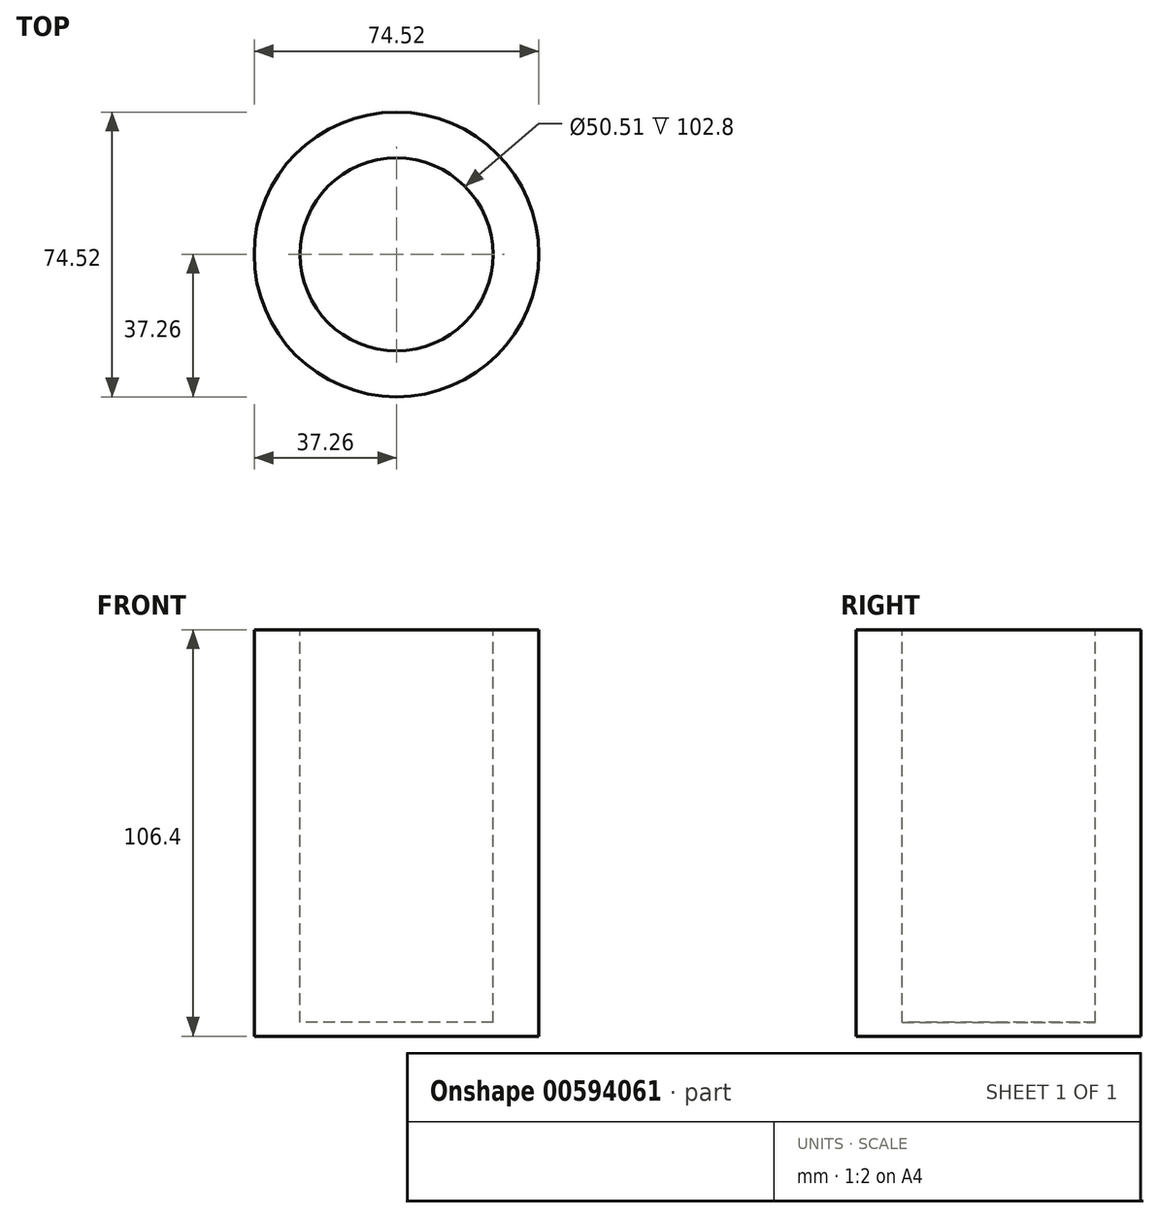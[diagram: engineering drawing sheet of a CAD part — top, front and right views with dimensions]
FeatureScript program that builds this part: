
annotation { "Feature Type Name" : "Feature", "Feature Type Description" : "" }
export const myFeature = defineFeature(function(context is Context, id is Id, definition is map)
    precondition{}
    {
        {
            var Q0;
            Q0=qCreatedBy(makeId("Top.planeOp"),FACE);
            var sketch = newSketch(context, id + "F0", { "sketchPlane" : qUnion([Q0])});
            skCircle(sketch, "E0", {"center": v(0, 0) * mm, "radius": 37.26 * mm});
            skSolve(sketch);
        }
        {
            var Q0;
            Q0 = qSketchRegion(id + "F2", true);
            var Q1;
            Q1=makeQuery(id+"F0.imprint","IMPRINT",FACE,{"disambiguationData":[TD([[makeQuery(id+"F0.imprint","IMPRINT",EDGE,{"derivedFrom":sQuery(id+"F0.wireOp",EDGE,"E0")}),1.0]])]});
            extrude(context, id + "F1", {"entities" : qUnion([Q0, Q1]), "depth" : 106.4 * mm, "offsetDistance" : 25 * mm});
        }
        {
            var Q0;
            Q0=makeQuery(id+"F1.opExtrude","CAP_FACE",FACE,{"disambiguationData":[OSD([sQuery(id+"F0.wireOp",EDGE,"E0")])],"isStart":false});
            var sketch = newSketch(context, id + "F2", { "sketchPlane" : qUnion([Q0])});
            skCircle(sketch, "E1.cCircle", {"center": v(0, 0) * mm, "radius": 28.44 * mm, "construction": true});
            skLineSegment(sketch, "E1.0", {"start": v(30.45, -12.3) * mm, "end": v(4.57, -32.52) * mm});
            skLineSegment(sketch, "E1.1", {"start": v(4.57, -32.52) * mm, "end": v(-25.88, -20.22) * mm});
            skLineSegment(sketch, "E1.2", {"start": v(-25.88, -20.22) * mm, "end": v(-30.45, 12.3) * mm});
            skLineSegment(sketch, "E1.3", {"start": v(-30.45, 12.3) * mm, "end": v(-4.57, 32.52) * mm});
            skLineSegment(sketch, "E1.4", {"start": v(-4.57, 32.52) * mm, "end": v(25.88, 20.22) * mm});
            skLineSegment(sketch, "E1.5", {"start": v(25.88, 20.22) * mm, "end": v(30.45, -12.3) * mm});
            skPoint(sketch, "E1.0.midPoint", {"position": v(17.51, -22.4) * mm});
            skSolve(sketch);
        }
        {
            var Q0;
            Q0=makeQuery(id+"F2.imprint","IMPRINT",FACE,{"disambiguationData":[TD([[makeQuery(id+"F2.imprint","IMPRINT",EDGE,{"derivedFrom":sQuery(id+"F2.wireOp",EDGE,"E1.0")}),-1.0]])]});
            extrude(context, id + "F3", {"entities" : qUnion([Q0]), "operationType" : NewBodyOperationType.ADD, "oppositeDirection" : true, "depth" : 86.5 * mm, "offsetDistance" : 25 * mm});
        }
        {
            var Q0;
            Q0=makeQuery(id+"F1.opExtrude","CAP_FACE",FACE,{"disambiguationData":[OSD([sQuery(id+"F0.wireOp",EDGE,"E0")])],"isStart":false});
            var sketch = newSketch(context, id + "F4", { "sketchPlane" : qUnion([Q0])});
            skSolve(sketch);
        }
        {
            var Q0;
            Q0=makeQuery(id+"F4.imprint","IMPRINT",FACE,{"disambiguationData":[TD([[makeQuery(id+"F4.imprint","IMPRINT",EDGE,{"derivedFrom":makeQuery(id+"F1.opExtrude","CAP_EDGE",EDGE,{"disambiguationData":[OSD([sQuery(id+"F0.wireOp",EDGE,"E0")])],"isStart":false})}),1.0]])]});
            var sketch = newSketch(context, id + "F5", { "sketchPlane" : qUnion([Q0])});
            skCircle(sketch, "E2", {"center": v(0, 0) * mm, "radius": 25.25 * mm});
            skSolve(sketch);
        }
        {
            var Q0;
            Q0 = qSketchRegion(id + "F5", true);
            extrude(context, id + "F6", {"entities" : qUnion([Q0]), "operationType" : NewBodyOperationType.REMOVE, "oppositeDirection" : true, "depth" : 102.8 * mm, "offsetDistance" : 25 * mm});
        }
    });
